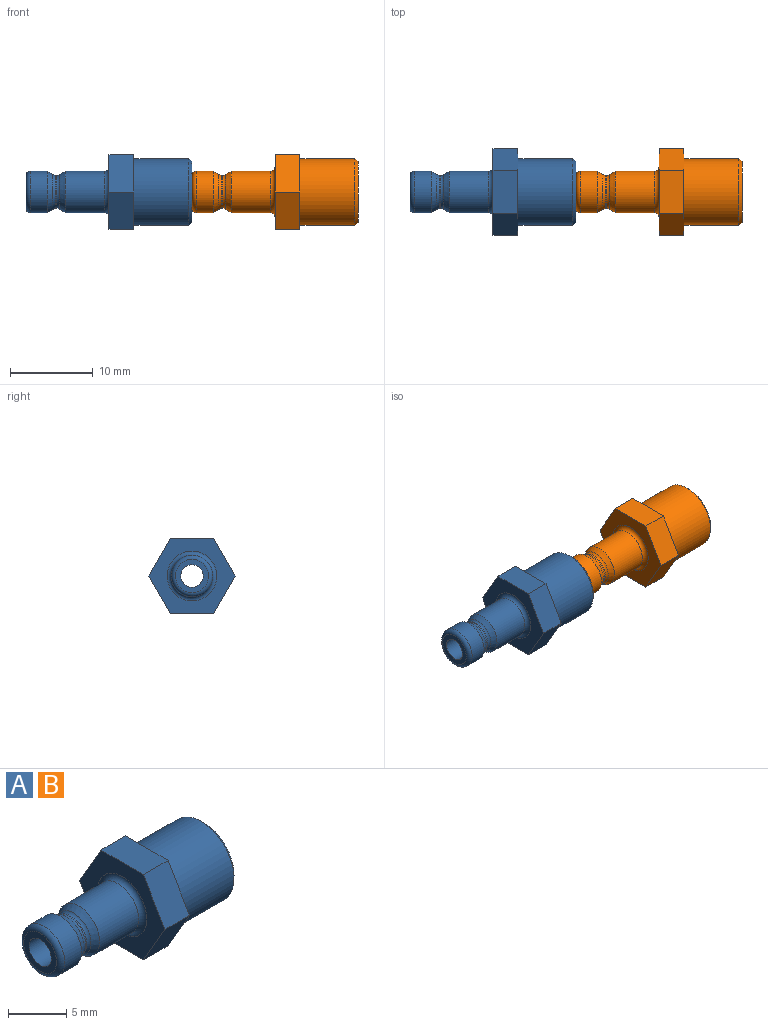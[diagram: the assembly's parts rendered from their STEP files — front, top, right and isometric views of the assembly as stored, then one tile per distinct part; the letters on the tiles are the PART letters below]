
ASSEMBLY  parts=2 mates=2
PART A: 23 faces, bbox 20x10.4x9 mm
  f0: cylinder r=4mm len=8mm, axis (1,0,0), area 166.5mm2, adj f1,f22
  f1: cone r=3.81mm half-angle=45deg, axis (-1,0,0), area 12.7mm2, adj f0,f15
  f2: torus R=3mm, axis (1,0,0), area 13.2mm2, adj f3,f14
  f3: cylinder r=2.5mm len=5mm, axis (1,0,0), area 74.6mm2, adj f2,f4
  f4: cone r=2.31mm half-angle=29.4deg, axis (1,0,0), area 11.2mm2, adj f3,f5
  f5: torus R=2.48mm, axis (1,0,0), area 5mm2, adj f4,f6
  f6: cylinder r=1.98mm len=3.95mm, axis (1,0,0), area 1.9mm2, adj f5,f7
  f7: torus R=2.48mm, axis (1,0,0), area 5mm2, adj f6,f8
  f8: cone r=2.31mm half-angle=29.4deg, axis (-1,0,0), area 11.2mm2, adj f7,f9
  f9: cylinder r=2.5mm len=5mm, axis (1,0,0), area 32.2mm2, adj f8,f10
  f10: torus R=2mm, axis (1,0,0), area 11.4mm2, adj f9,f13
  f11: cylinder r=1.35mm len=19mm, axis (1,0,0), area 161.1mm2, adj f12,f13
  f12: cone r=0.97mm half-angle=30deg, axis (1,0,0), area 12mm2, adj f11,f15
  f13: plane 4x4mm, normal (-1,0,0), area 6.8mm2, adj f10,f11
  f14: plane 10.39x9mm, normal (-1,0,0), area 41.9mm2, adj f2,f16,f17,f18,f19,f20,f21
  f15: plane 7.25x7.25mm, normal (1,0,0), area 29.6mm2, adj f1,f12
  f16: plane 5.2x3mm, normal (0,0,1), area 15.6mm2, adj f14,f17,f21,f22
  f17: plane 4.5x3mm, normal (0,-0.87,0.5), area 15.6mm2, adj f14,f16,f18,f22
  f18: plane 4.5x3mm, normal (0,-0.87,-0.5), area 15.6mm2, adj f14,f17,f19,f22
  f19: plane 5.2x3mm, normal (0,0,-1), area 15.6mm2, adj f14,f18,f20,f22
  f20: plane 4.5x3mm, normal (0,0.87,-0.5), area 15.6mm2, adj f14,f19,f21,f22
  f21: plane 4.5x3mm, normal (0,0.87,0.5), area 15.6mm2, adj f14,f16,f20,f22
  f22: plane 10.39x9mm, normal (1,0,0), area 19.9mm2, adj f0,f16,f17,f18,f19,f20,f21
PART B: same geometry as A
PLACE A t=(-6.5,16.9,8.2)mm
PLACE B t=(13.5,16.9,8.2)mm
MATE parallel B.f0 <-> A.f0  axis (1,0,0) through (24.6,16.9,8.2)mm
MATE fastened B.f0 <-> A.f0  axis (-1,0,0) through (4.6,16.9,8.2)mm
